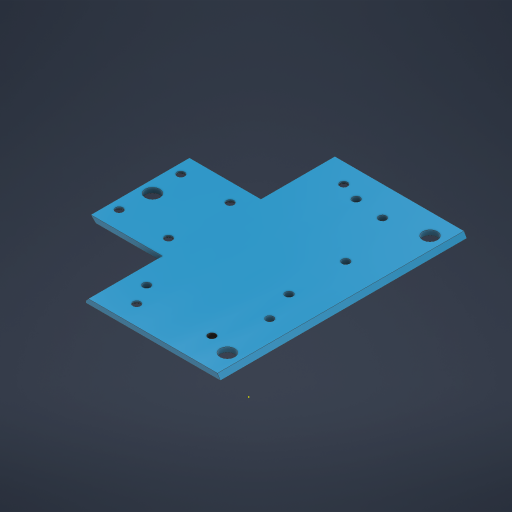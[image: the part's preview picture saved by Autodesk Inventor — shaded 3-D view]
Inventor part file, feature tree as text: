
AUTODESK INVENTOR PART (.ipt)
format: ipt  version: 2024 (Build 280153000, 153)  size: 303,616 bytes
history: native  units: in
note: dims shown in document units (in); Inventor stores cm internally (conversion verified against a paired STEP export)
features: sketch x8, hole x5, chamfer x4, extrude x2, plane x1, projected_geometry x1
ambient origin geometry x8: Origin, YZ Plane, XZ Plane, XY Plane, X Axis, Y Axis, Z Axis, Center Point
bodies: Solid1 (feature_tree)
feature tree (21):
  extrude  "Extrusion1"  Depth=1.1811in
  plane  "Work Plane1"
  hole  "Hole1"  [1 undecoded]
  chamfer  "Chamfer1"  Distance=0.0787in Angle=45.0deg
  chamfer  "Chamfer2"  Distance=0.0787in Angle=45.0deg
  extrude  "Extrusion2"  Depth=0.2362in
  chamfer  "Chamfer3"  Distance=4.7244in
  hole  "Hole2"  [1 undecoded]
  chamfer  "Chamfer4"  Distance=1.6512in
  hole  "Hole3"  [1 undecoded]
  sketch  "Sketch7"  dims[d27=3.7008in d28=0.0394in d29=0.0472in d30=45.0deg]
  hole  "Hole4"  [1 undecoded]
  hole  "Hole6"  [1 undecoded]
  sketch  "Sketch1"  dims[d0=3.937in d2=1.1811in]
  sketch  "Sketch2"  dims[d4=1.5748in d5=0.0787in d6=0.0in]
  sketch  "Sketch3"  dims[d7=2.5984in]
  sketch  "Sketch4"  dims[d9=0.122in d10=0.2362in d11=0.1575in d12=0.0787in d13=90.0deg d14=0.315in d15=0.8108in d16=0.0591in d17=0.0787in d18=45.0deg d19=0.0787in d20=0.0787in d21=45.0deg]
  sketch  "Sketch6"  dims[d22=0.315in d23=120.0deg d24=0.2362in d25=4.7244in d26=0.0in]
  projected_geometry  "Projected Loop1"
  sketch  "Sketch8"  dims[d31=0.315in]
  sketch  "Sketch10"  dims[d32=1.6512in d33=1.6512in d34=0.315in d35=3.937in d36=0.122in d37=0.2362in d38=0.1575in d39=0.0787in d40=90.0deg d41=0.315in d42=0.8108in d43=0.0591in d44=0.0787in d45=45.0deg d46=0.122in d47=0.2362in d48=0.1575in d49=0.0787in d50=90.0deg d51=0.315in d52=0.8108in d56=1.3661in d57=1.664in d61=0.2362in d62=0.2362in d63=0.1575in d64=0.0787in d65=90.0deg d66=0.315in d67=0.8108in d75=0.122in d76=0.2362in d77=0.1575in d78=0.0787in d79=90.0deg d80=0.315in d81=0.8108in d83=0.8302in d84=0.4724in d85=0.4724in d87=0.5619in d88=0.5674in d89=0.5674in d53=0.0295in d54=0.8108in d55=0.0025in]
note: 5 required parameter values undecoded (feature->parameter linkage not recoverable at this tier; creation-order binding heuristic only, values carry confidence <= 0.55)
